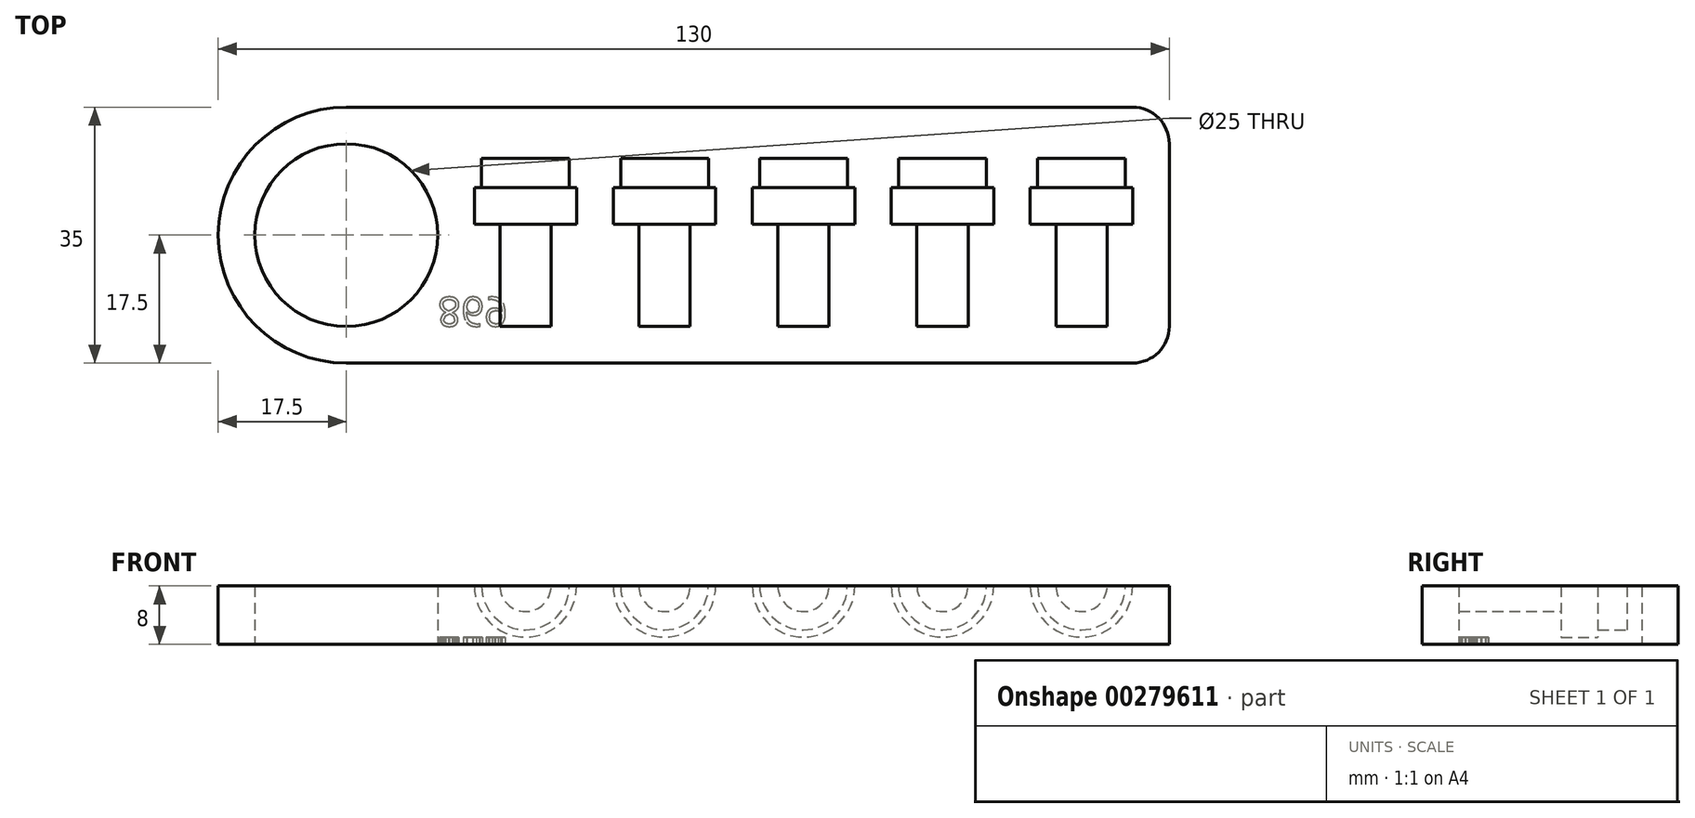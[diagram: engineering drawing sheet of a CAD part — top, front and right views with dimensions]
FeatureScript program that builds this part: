
annotation { "Feature Type Name" : "Feature", "Feature Type Description" : "" }
export const myFeature = defineFeature(function(context is Context, id is Id, definition is map)
    precondition{}
    {
        {
            var Q0;
            Q0=qCreatedBy(makeId("Top.planeOp"),FACE);
            var sketch = newSketch(context, id + "F0", { "sketchPlane" : qUnion([Q0])});
            skLineSegment(sketch, "E0.bottom", {"start": v(17.5, 0) * mm, "end": v(125, 0) * mm});
            skLineSegment(sketch, "E0.top", {"start": v(17.5, 35) * mm, "end": v(125, 35) * mm});
            skLineSegment(sketch, "E0.left", {"start": v(0, 17.5) * mm, "end": v(0, 17.5) * mm});
            skLineSegment(sketch, "E0.right", {"start": v(130, 5) * mm, "end": v(130, 30) * mm});
            skLineSegment(sketch, "E1.bottom", {"start": v(0, 0) * mm, "end": v(17.5, 0) * mm, "construction": true});
            skLineSegment(sketch, "E1.top", {"start": v(0, 17.5) * mm, "end": v(17.5, 17.5) * mm, "construction": true});
            skLineSegment(sketch, "E1.left", {"start": v(0, 0) * mm, "end": v(0, 17.5) * mm, "construction": true});
            skLineSegment(sketch, "E1.right", {"start": v(17.5, 0) * mm, "end": v(17.5, 17.5) * mm, "construction": true});
            skCircle(sketch, "E2", {"center": v(17.5, 17.5) * mm, "radius": 12.5 * mm});
            skPoint(sketch, "E3.visualSharp", {"position": v(0, 0) * mm});
            skArc(sketch, "E3.filletArc", {"start": v(0, 17.5) * mm, "mid": v(5.13, 5.13) * mm, "end": v(17.5, 0) * mm});
            skPoint(sketch, "E4.visualSharp", {"position": v(0, 35) * mm});
            skArc(sketch, "E4.filletArc", {"start": v(17.5, 35) * mm, "mid": v(5.13, 29.87) * mm, "end": v(0, 17.5) * mm});
            skPoint(sketch, "E5.visualSharp", {"position": v(130, 35) * mm});
            skArc(sketch, "E5.filletArc", {"start": v(130, 30) * mm, "mid": v(128.54, 33.54) * mm, "end": v(125, 35) * mm});
            skPoint(sketch, "E6.visualSharp", {"position": v(130, 0) * mm});
            skArc(sketch, "E6.filletArc", {"start": v(125, 0) * mm, "mid": v(128.54, 1.46) * mm, "end": v(130, 5) * mm});
            skSolve(sketch);
        }
        {
            var Q0;
            Q0=makeQuery(id+"F0.imprint","IMPRINT",FACE,{"disambiguationData":[TD([[makeQuery(id+"F0.imprint","IMPRINT",EDGE,{"derivedFrom":sQuery(id+"F0.wireOp",EDGE,"E0.bottom")}),1.0]])]});
            extrude(context, id + "F1", {"entities" : qUnion([Q0]), "depth" : 8 * mm});
        }
        {
            var Q0;
            Q0=makeQuery(id+"F1.opExtrude","CAP_FACE",FACE,{"disambiguationData":[OSD([sQuery(id+"F0.wireOp",EDGE,"E0.bottom"),sQuery(id+"F0.wireOp",EDGE,"E0.top"),sQuery(id+"F0.wireOp",EDGE,"E0.right"),sQuery(id+"F0.wireOp",EDGE,"E2"),sQuery(id+"F0.wireOp",EDGE,"E3.filletArc"),sQuery(id+"F0.wireOp",EDGE,"E4.filletArc"),sQuery(id+"F0.wireOp",EDGE,"E5.filletArc"),sQuery(id+"F0.wireOp",EDGE,"E6.filletArc")])],"isStart":false});
            var sketch = newSketch(context, id + "F2", { "sketchPlane" : qUnion([Q0])});
            skLineSegment(sketch, "E7.bottom", {"start": v(0, 0) * mm, "end": v(42, 0) * mm, "construction": true});
            skLineSegment(sketch, "E7.top", {"start": v(0, 5) * mm, "end": v(42, 5) * mm, "construction": true});
            skLineSegment(sketch, "E7.left", {"start": v(0, 0) * mm, "end": v(0, 5) * mm, "construction": true});
            skLineSegment(sketch, "E7.right", {"start": v(42, 0) * mm, "end": v(42, 5) * mm, "construction": true});
            skLineSegment(sketch, "E8", {"start": v(42, 5) * mm, "end": v(61, 5) * mm, "construction": true});
            skLineSegment(sketch, "E9", {"start": v(61, 5) * mm, "end": v(80, 5) * mm, "construction": true});
            skLineSegment(sketch, "E10", {"start": v(80, 5) * mm, "end": v(99, 5) * mm, "construction": true});
            skLineSegment(sketch, "E11.bottom", {"start": v(42, 5) * mm, "end": v(45.5, 5) * mm});
            skLineSegment(sketch, "E11.left", {"start": v(42, 5) * mm, "end": v(42, 19) * mm});
            skLineSegment(sketch, "E11.right", {"start": v(45.5, 5) * mm, "end": v(45.5, 19) * mm});
            skLineSegment(sketch, "E12.bottom", {"start": v(45.5, 19) * mm, "end": v(49, 19) * mm});
            skLineSegment(sketch, "E12.top", {"start": v(48, 24) * mm, "end": v(49, 24) * mm});
            skLineSegment(sketch, "E12.left", {"start": v(42, 19) * mm, "end": v(42, 24) * mm});
            skLineSegment(sketch, "E12.right", {"start": v(49, 19) * mm, "end": v(49, 24) * mm});
            skLineSegment(sketch, "E13.top", {"start": v(42, 28) * mm, "end": v(48, 28) * mm});
            skLineSegment(sketch, "E13.left", {"start": v(42, 24) * mm, "end": v(42, 28) * mm});
            skLineSegment(sketch, "E13.right", {"start": v(48, 24) * mm, "end": v(48, 28) * mm});
            skLineSegment(sketch, "E14.bottom", {"start": v(61, 5) * mm, "end": v(64.5, 5) * mm});
            skLineSegment(sketch, "E14.left", {"start": v(61, 5) * mm, "end": v(61, 19) * mm});
            skLineSegment(sketch, "E14.right", {"start": v(64.5, 5) * mm, "end": v(64.5, 19) * mm});
            skLineSegment(sketch, "E15.bottom", {"start": v(64.5, 19) * mm, "end": v(68, 19) * mm});
            skLineSegment(sketch, "E15.top", {"start": v(67, 24) * mm, "end": v(68, 24) * mm});
            skLineSegment(sketch, "E15.left", {"start": v(61, 19) * mm, "end": v(61, 24) * mm});
            skLineSegment(sketch, "E15.right", {"start": v(68, 19) * mm, "end": v(68, 24) * mm});
            skLineSegment(sketch, "E16.top", {"start": v(61, 28) * mm, "end": v(67, 28) * mm});
            skLineSegment(sketch, "E16.left", {"start": v(61, 24) * mm, "end": v(61, 28) * mm});
            skLineSegment(sketch, "E16.right", {"start": v(67, 24) * mm, "end": v(67, 28) * mm});
            skLineSegment(sketch, "E17.bottom", {"start": v(80, 5) * mm, "end": v(83.5, 5) * mm});
            skLineSegment(sketch, "E17.left", {"start": v(80, 5) * mm, "end": v(80, 19) * mm});
            skLineSegment(sketch, "E17.right", {"start": v(83.5, 5) * mm, "end": v(83.5, 19) * mm});
            skLineSegment(sketch, "E18.bottom", {"start": v(83.5, 19) * mm, "end": v(87, 19) * mm});
            skLineSegment(sketch, "E18.top", {"start": v(86, 24) * mm, "end": v(87, 24) * mm});
            skLineSegment(sketch, "E18.left", {"start": v(80, 19) * mm, "end": v(80, 24) * mm});
            skLineSegment(sketch, "E18.right", {"start": v(87, 19) * mm, "end": v(87, 24) * mm});
            skLineSegment(sketch, "E19.top", {"start": v(80, 28) * mm, "end": v(86, 28) * mm});
            skLineSegment(sketch, "E19.left", {"start": v(80, 24) * mm, "end": v(80, 28) * mm});
            skLineSegment(sketch, "E19.right", {"start": v(86, 24) * mm, "end": v(86, 28) * mm});
            skLineSegment(sketch, "E20.bottom", {"start": v(99, 5) * mm, "end": v(102.5, 5) * mm});
            skLineSegment(sketch, "E20.left", {"start": v(99, 5) * mm, "end": v(99, 19) * mm});
            skLineSegment(sketch, "E20.right", {"start": v(102.5, 5) * mm, "end": v(102.5, 19) * mm});
            skLineSegment(sketch, "E21.bottom", {"start": v(102.5, 19) * mm, "end": v(106, 19) * mm});
            skLineSegment(sketch, "E21.top", {"start": v(105, 24) * mm, "end": v(106, 24) * mm});
            skLineSegment(sketch, "E21.left", {"start": v(99, 19) * mm, "end": v(99, 24) * mm});
            skLineSegment(sketch, "E21.right", {"start": v(106, 19) * mm, "end": v(106, 24) * mm});
            skLineSegment(sketch, "E22.top", {"start": v(99, 28) * mm, "end": v(105, 28) * mm});
            skLineSegment(sketch, "E22.left", {"start": v(99, 24) * mm, "end": v(99, 28) * mm});
            skLineSegment(sketch, "E22.right", {"start": v(105, 24) * mm, "end": v(105, 28) * mm});
            skLineSegment(sketch, "E23", {"start": v(99, 5) * mm, "end": v(118, 5) * mm, "construction": true});
            skLineSegment(sketch, "E24.bottom", {"start": v(118, 5) * mm, "end": v(121.5, 5) * mm});
            skLineSegment(sketch, "E24.left", {"start": v(118, 5) * mm, "end": v(118, 19) * mm});
            skLineSegment(sketch, "E24.right", {"start": v(121.5, 5) * mm, "end": v(121.5, 19) * mm});
            skLineSegment(sketch, "E25.bottom", {"start": v(121.5, 19) * mm, "end": v(125, 19) * mm});
            skLineSegment(sketch, "E25.top", {"start": v(124, 24) * mm, "end": v(125, 24) * mm});
            skLineSegment(sketch, "E25.left", {"start": v(118, 19) * mm, "end": v(118, 24) * mm});
            skLineSegment(sketch, "E25.right", {"start": v(125, 19) * mm, "end": v(125, 24) * mm});
            skLineSegment(sketch, "E26.top", {"start": v(118, 28) * mm, "end": v(124, 28) * mm});
            skLineSegment(sketch, "E26.left", {"start": v(118, 24) * mm, "end": v(118, 28) * mm});
            skLineSegment(sketch, "E26.right", {"start": v(124, 24) * mm, "end": v(124, 28) * mm});
            skSolve(sketch);
        }
        {
            var Q0;
            Q0=makeQuery(id+"F2.imprint","IMPRINT",FACE,{"disambiguationData":[TD([[makeQuery(id+"F2.imprint","IMPRINT",EDGE,{"derivedFrom":sQuery(id+"F2.wireOp",EDGE,"E11.bottom")}),1.0]])]});
            var Q1;
            Q1=sQuery(id+"F2.wireOp",EDGE,"E12.left");
            revolve(context, id + "F3", {"operationType" : NewBodyOperationType.REMOVE, "entities" : qUnion([Q0]), "axis" : qUnion([Q1]), "revolveType" : RevolveType.FULL, "oppositeDirection" : true});
        }
        {
            var Q0;
            Q0=makeQuery(id+"F2.imprint","IMPRINT",FACE,{"disambiguationData":[TD([[makeQuery(id+"F2.imprint","IMPRINT",EDGE,{"derivedFrom":sQuery(id+"F2.wireOp",EDGE,"E14.bottom")}),1.0]])]});
            var Q1;
            Q1=sQuery(id+"F2.wireOp",EDGE,"E15.left");
            revolve(context, id + "F4", {"operationType" : NewBodyOperationType.REMOVE, "entities" : qUnion([Q0]), "axis" : qUnion([Q1]), "revolveType" : RevolveType.FULL, "oppositeDirection" : true});
        }
        {
            var Q0;
            Q0=makeQuery(id+"F2.imprint","IMPRINT",FACE,{"disambiguationData":[TD([[makeQuery(id+"F2.imprint","IMPRINT",EDGE,{"derivedFrom":sQuery(id+"F2.wireOp",EDGE,"E17.bottom")}),1.0]])]});
            var Q1;
            Q1=sQuery(id+"F2.wireOp",EDGE,"E17.left");
            revolve(context, id + "F5", {"operationType" : NewBodyOperationType.REMOVE, "entities" : qUnion([Q0]), "axis" : qUnion([Q1]), "revolveType" : RevolveType.FULL, "oppositeDirection" : true});
        }
        {
            var Q0;
            Q0=makeQuery(id+"F2.imprint","IMPRINT",FACE,{"disambiguationData":[TD([[makeQuery(id+"F2.imprint","IMPRINT",EDGE,{"derivedFrom":sQuery(id+"F2.wireOp",EDGE,"E20.bottom")}),1.0]])]});
            var Q1;
            Q1=sQuery(id+"F2.wireOp",EDGE,"E20.left");
            revolve(context, id + "F6", {"operationType" : NewBodyOperationType.REMOVE, "entities" : qUnion([Q0]), "axis" : qUnion([Q1]), "revolveType" : RevolveType.FULL, "oppositeDirection" : true});
        }
        {
            var Q0;
            Q0=makeQuery(id+"F2.imprint","IMPRINT",FACE,{"disambiguationData":[TD([[makeQuery(id+"F2.imprint","IMPRINT",EDGE,{"derivedFrom":sQuery(id+"F2.wireOp",EDGE,"E24.bottom")}),1.0]])]});
            var Q1;
            Q1=sQuery(id+"F2.wireOp",EDGE,"E24.left");
            revolve(context, id + "F7", {"operationType" : NewBodyOperationType.REMOVE, "entities" : qUnion([Q0]), "axis" : qUnion([Q1]), "revolveType" : RevolveType.FULL, "oppositeDirection" : true});
        }
        {
            var Q0;
            Q0=makeQuery(id+"F1.opExtrude","CAP_FACE",FACE,{"disambiguationData":[OSD([sQuery(id+"F0.wireOp",EDGE,"E0.bottom"),sQuery(id+"F0.wireOp",EDGE,"E0.top"),sQuery(id+"F0.wireOp",EDGE,"E0.right"),sQuery(id+"F0.wireOp",EDGE,"E2"),sQuery(id+"F0.wireOp",EDGE,"E3.filletArc"),sQuery(id+"F0.wireOp",EDGE,"E4.filletArc"),sQuery(id+"F0.wireOp",EDGE,"E5.filletArc"),sQuery(id+"F0.wireOp",EDGE,"E6.filletArc")])],"isStart":true});
            var sketch = newSketch(context, id + "F8", { "sketchPlane" : qUnion([Q0])});
            skLineSegment(sketch, "E27.bottom", {"start": v(0, 0) * mm, "end": v(30, 0) * mm, "construction": true});
            skLineSegment(sketch, "E27.top", {"start": v(0, -5) * mm, "end": v(30, -5) * mm, "construction": true});
            skLineSegment(sketch, "E27.left", {"start": v(0, 0) * mm, "end": v(0, -5) * mm, "construction": true});
            skLineSegment(sketch, "E27.right", {"start": v(30, 0) * mm, "end": v(30, -5) * mm, "construction": true});
            skText(sketch, "E28", { "text": "869", "fontName": "OpenSans-Regular.ttf"});
            const initialGuessF8  = {"E28": [0.03, -0.009, 1, 0, 0.004]};
            skSetInitialGuess(sketch, initialGuessF8);
            skSolve(sketch);
        }
        {
            var Q0;
            Q0 = qSketchRegion(id + "F8", true);
            extrude(context, id + "F9", {"entities" : qUnion([Q0]), "operationType" : NewBodyOperationType.REMOVE, "oppositeDirection" : true, "depth" : 1 * mm});
        }
    });
